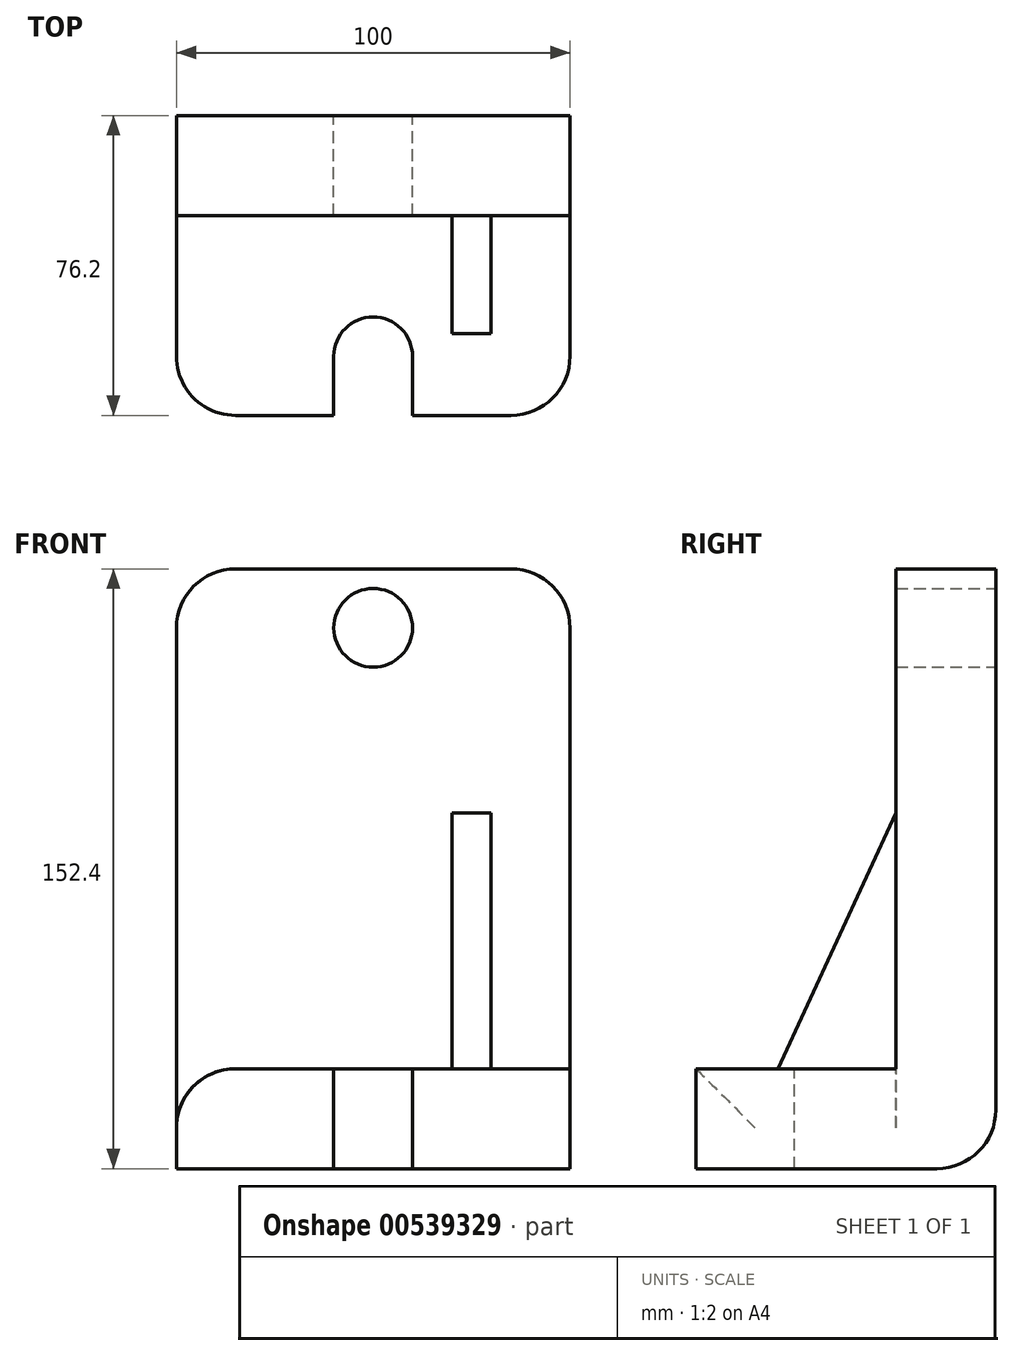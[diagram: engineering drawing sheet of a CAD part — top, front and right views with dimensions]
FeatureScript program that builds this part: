
annotation { "Feature Type Name" : "Feature", "Feature Type Description" : "" }
export const myFeature = defineFeature(function(context is Context, id is Id, definition is map)
    precondition{}
    {
        {
            var Q0;
            Q0=qCreatedBy(makeId("Right.planeOp"),FACE);
            var sketch = newSketch(context, id + "F0", { "sketchPlane" : qUnion([Q0])});
            skLineSegment(sketch, "E0", {"start": v(0, 0) * mm, "end": v(0, 152.4) * mm});
            skLineSegment(sketch, "E1", {"start": v(0, 152.4) * mm, "end": v(-25.4, 152.4) * mm});
            skLineSegment(sketch, "E2", {"start": v(-25.4, 152.4) * mm, "end": v(-25.4, 25.4) * mm});
            skLineSegment(sketch, "E3", {"start": v(-25.4, 25.4) * mm, "end": v(-76.2, 25.4) * mm});
            skLineSegment(sketch, "E4", {"start": v(-76.2, 25.4) * mm, "end": v(-76.2, 0) * mm});
            skLineSegment(sketch, "E5", {"start": v(-76.2, 0) * mm, "end": v(0, 0) * mm});
            skSolve(sketch);
        }
        {
            var Q0;
            Q0=makeQuery(id+"F0.imprint","IMPRINT",FACE,{"disambiguationData":[TD([[makeQuery(id+"F0.imprint","IMPRINT",EDGE,{"derivedFrom":sQuery(id+"F0.wireOp",EDGE,"E0")}),1.0]])]});
            extrude(context, id + "F1", {"entities" : qUnion([Q0]), "endBound" : BoundingType.SYMMETRIC, "depth" : 100 * mm, "offsetDistance" : 25.4 * mm});
        }
        {
            var Q0;
            Q0=makeQuery(id+"F1.opExtrude","SWEPT_FACE",FACE,{"disambiguationData":[OSD([sQuery(id+"F0.wireOp",EDGE,"E0")])]});
            var sketch = newSketch(context, id + "F2", { "sketchPlane" : qUnion([Q0])});
            skCircle(sketch, "E6", {"center": v(0, 137.4) * mm, "radius": 10 * mm});
            skSolve(sketch);
        }
        {
            var Q0;
            Q0=makeQuery(id+"F1.opExtrude","SWEPT_FACE",FACE,{"disambiguationData":[OSD([sQuery(id+"F0.wireOp",EDGE,"E3")])]});
            var sketch = newSketch(context, id + "F3", { "sketchPlane" : qUnion([Q0])});
            skCircle(sketch, "E7", {"center": v(0, -61.2) * mm, "radius": 10 * mm});
            skLineSegment(sketch, "E8", {"start": v(-10, -61.2) * mm, "end": v(-10, -76.2) * mm});
            skLineSegment(sketch, "E9", {"start": v(10, -61.2) * mm, "end": v(10, -76.2) * mm});
            skSolve(sketch);
        }
        {
            var Q0;
            {var subQ0=sQuery(id+"F3.wireOp",EDGE,"E7");var subQ1=makeQuery(id+"F3.imprint","INTERSECT",VERTEX,{"derivedFrom":[subQ0,sQuery(id+"F3.wireOp",EDGE,"E8")]});Q0=makeQuery(id+"F3.imprint","IMPRINT",FACE,{"disambiguationData":[TD([[makeQuery(id+"F3.imprint","IMPRINT",EDGE,{"disambiguationData":[TD([[subQ1,1.0]])],"derivedFrom":subQ0}),1.0]])]});}
            var Q1;
            {var subQ0=sQuery(id+"F3.wireOp",EDGE,"E8");Q1=makeQuery(id+"F3.imprint","IMPRINT",FACE,{"disambiguationData":[TD([[makeQuery(id+"F3.imprint","IMPRINT",EDGE,{"derivedFrom":subQ0}),1.0]])]});}
            extrude(context, id + "F4", {"entities" : qUnion([Q0, Q1]), "operationType" : NewBodyOperationType.REMOVE, "endBound" : BoundingType.THROUGH_ALL, "oppositeDirection" : true, "depth" : 25 * mm, "offsetDistance" : 25 * mm});
        }
        {
            var Q0;
            Q0=makeQuery(id+"F2.imprint","IMPRINT",FACE,{"disambiguationData":[TD([[makeQuery(id+"F2.imprint","IMPRINT",EDGE,{"derivedFrom":sQuery(id+"F2.wireOp",EDGE,"E6")}),1.0]])]});
            extrude(context, id + "F5", {"entities" : qUnion([Q0]), "operationType" : NewBodyOperationType.REMOVE, "endBound" : BoundingType.THROUGH_ALL, "oppositeDirection" : true, "depth" : 25 * mm, "offsetDistance" : 25 * mm});
        }
        {
            var Q0;
            Q0=qCreatedBy(makeId("Right.planeOp"),FACE);
            cPlane(context, id + "F6", {"entities" : qUnion([Q0]), "cplaneType" : CPlaneType.OFFSET, "offset" : 25 * mm, "width" : 150 * mm, "height" : 150 * mm});
        }
        {
            var Q0;
            Q0=qCreatedBy(id+"F6.planeOp",FACE);
            var sketch = newSketch(context, id + "F7", { "sketchPlane" : qUnion([Q0])});
            skPoint(sketch, "E10.0", {"position": v(-25.4, 90.4) * mm});
            skLineSegment(sketch, "E11.0", {"start": v(-25.4, 90.4) * mm, "end": v(-25.4, 25.4) * mm});
            skLineSegment(sketch, "E11.1", {"start": v(-25.4, 25.4) * mm, "end": v(-55.4, 25.4) * mm});
            skLineSegment(sketch, "E12", {"start": v(-25.4, 90.4) * mm, "end": v(-55.4, 25.4) * mm});
            skSolve(sketch);
        }
        {
            var Q0;
            Q0=makeQuery(id+"F7.imprint","IMPRINT",FACE,{"disambiguationData":[TD([[makeQuery(id+"F7.imprint","IMPRINT",EDGE,{"derivedFrom":sQuery(id+"F7.wireOp",EDGE,"E11.0")}),-1.0]])]});
            extrude(context, id + "F8", {"entities" : qUnion([Q0]), "operationType" : NewBodyOperationType.ADD, "endBound" : BoundingType.SYMMETRIC, "depth" : 10 * mm, "offsetDistance" : 25 * mm});
        }
        {
            var Q0;
            Q0=makeQuery(id+"F1.opExtrude","SWEPT_FACE",FACE,{"disambiguationData":[OSD([sQuery(id+"F0.wireOp",EDGE,"E2")])]});
            var sketch = newSketch(context, id + "F9", { "sketchPlane" : qUnion([Q0])});
            skCircle(sketch, "E13", {"center": v(0, 137.4) * mm, "radius": 12.5 * mm});
            skSolve(sketch);
        }
        {
            var Q0;
            Q0=makeQuery(id+"F9.imprint","IMPRINT",FACE,{"disambiguationData":[TD([[makeQuery(id+"F9.imprint","IMPRINT",EDGE,{"derivedFrom":makeQuery(id+"F5.boolean.opBoolean","INTERSECT",EDGE,{"derivedFrom":[makeQuery(id+"F1.opExtrude","SWEPT_FACE",FACE,{"disambiguationData":[OSD([sQuery(id+"F0.wireOp",EDGE,"E2")])]}),makeQuery(id+"F5.opExtrude","SWEPT_FACE",FACE,{"disambiguationData":[OSD([sQuery(id+"F2.wireOp",EDGE,"E6")])]})]})}),-1.0]])]});
            extrude(context, id + "F10", {"entities" : qUnion([Q0]), "operationType" : NewBodyOperationType.REMOVE, "oppositeDirection" : true, "depth" : 3.9 * mm, "offsetDistance" : 25 * mm});
        }
        {
            var Q0;
            Q0=makeQuery(id+"F1.opExtrude","CAP_EDGE",EDGE,{"disambiguationData":[OSD([sQuery(id+"F0.wireOp",EDGE,"E1")])],"isStart":true});
            var Q1;
            Q1=makeQuery(id+"F1.opExtrude","CAP_EDGE",EDGE,{"disambiguationData":[OSD([sQuery(id+"F0.wireOp",EDGE,"E1")])],"isStart":false});
            var Q2;
            Q2=makeQuery(id+"F1.opExtrude","SWEPT_EDGE",EDGE,{"disambiguationData":[OSD([sQuery(id+"F0.wireOp",EDGE,"E0"),sQuery(id+"F0.wireOp",EDGE,"E5")])]});
            var Q3;
            Q3=makeQuery(id+"F1.opExtrude","CAP_EDGE",EDGE,{"disambiguationData":[OSD([sQuery(id+"F0.wireOp",EDGE,"E4")])],"isStart":false});
            var Q4;
            Q4=makeQuery(id+"F1.opExtrude","CAP_EDGE",EDGE,{"disambiguationData":[OSD([sQuery(id+"F0.wireOp",EDGE,"E4")])],"isStart":true});
            var Q5;
            Q5=makeQuery(id+"F1.opExtrude","CAP_EDGE",EDGE,{"disambiguationData":[OSD([sQuery(id+"F0.wireOp",EDGE,"E3")])],"isStart":true});
            fillet(context, id + "F11", {"entities" : qUnion([Q0, Q1, Q2, Q3, Q4, Q5]), "radius" : 15 * mm, "tangentPropagation" : true, "allowEdgeOverflow" : false});
        }
    });
